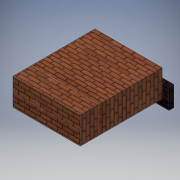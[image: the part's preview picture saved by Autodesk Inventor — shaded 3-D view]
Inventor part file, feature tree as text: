
AUTODESK INVENTOR PART (.ipt)
format: ipt  version: 2019 (Build 230136000, 136)  size: 190,464 bytes
history: native  units: mm
features: extrude x5, sketch x4, projected_geometry x3, other x2
ambient origin geometry x8: Origin, YZ Plane, XZ Plane, XY Plane, X Axis, Y Axis, Z Axis, Center Point
bodies: Body1 (feature_tree), Body2 (feature_tree)
feature tree (14):
  other  "Твердое тело1"
  extrude  "Выдавливание1"  Depth=1500.0mm
  extrude  "Выдавливание2"  Depth=375.0mm
  extrude  "Выдавливание3"  Depth=90.0mm TaperAngle=0.0deg
  sketch  "Эскиз4"
  extrude  "Выдавливание4"  Depth=1250.0mm
  extrude  "Выдавливание5"  Depth=500.0mm
  sketch  "Эскиз1"
  sketch  "Эскиз2"
  projected_geometry  "Спроецированная петля1"
  other  "Твердое тело2"
  sketch  "Эскиз3"
  projected_geometry  "Спроецированная петля2"
  projected_geometry  "Спроецированная петля3"
